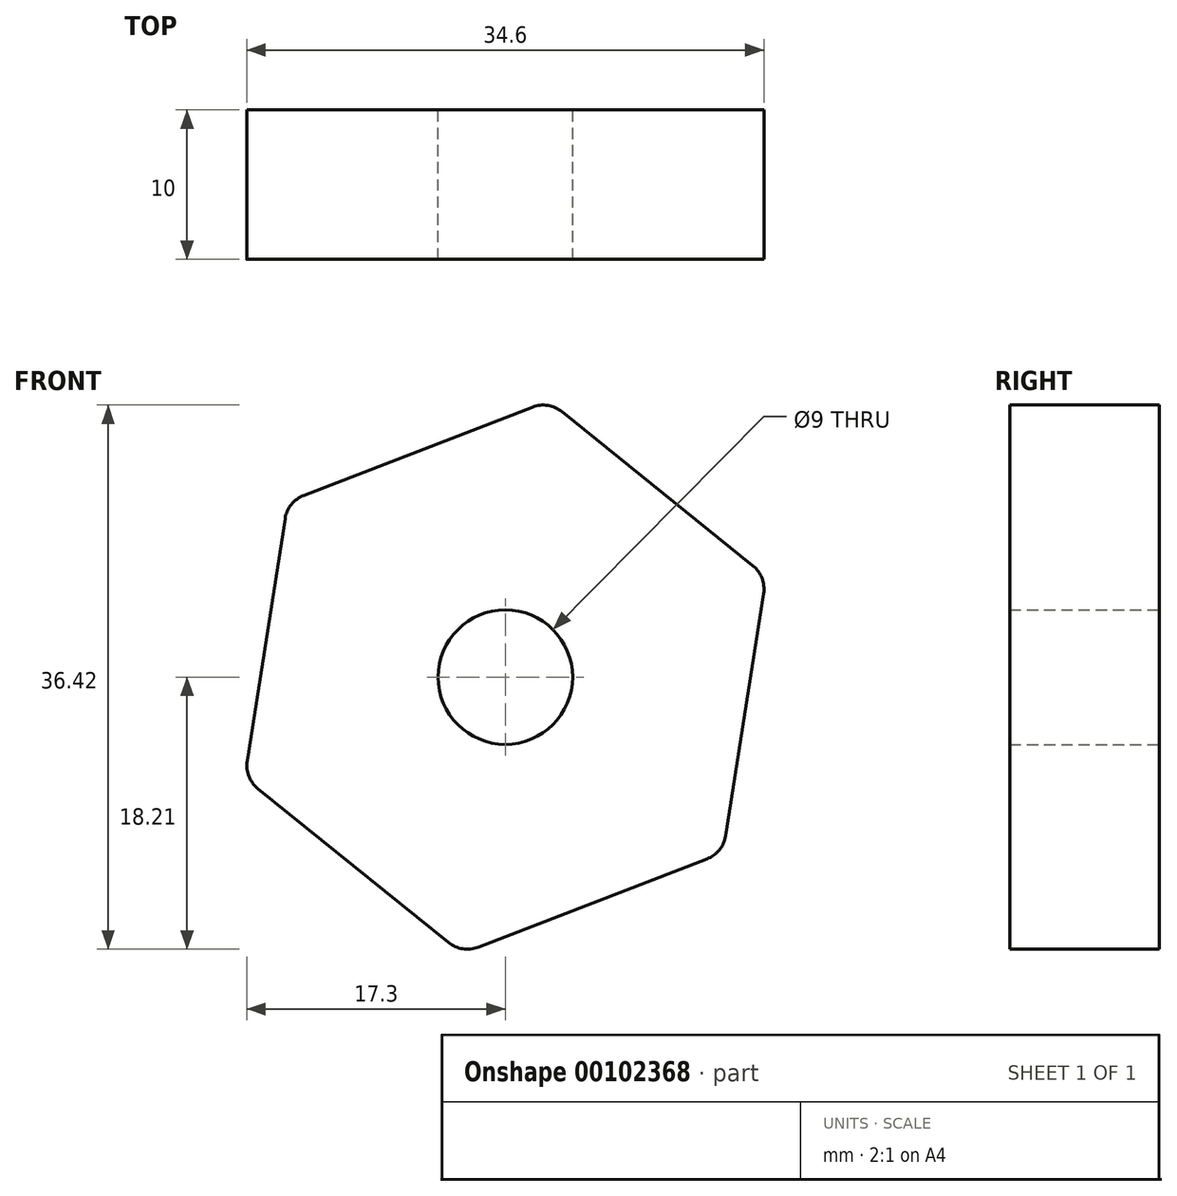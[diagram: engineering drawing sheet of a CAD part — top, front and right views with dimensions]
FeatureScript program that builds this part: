
annotation { "Feature Type Name" : "Feature", "Feature Type Description" : "" }
export const myFeature = defineFeature(function(context is Context, id is Id, definition is map)
    precondition{}
    {
        {
            var Q0;
            Q0=qCreatedBy(makeId("Front.planeOp"),FACE);
            var sketch = newSketch(context, id + "F0", { "sketchPlane" : qUnion([Q0])});
            skCircle(sketch, "E0", {"center": v(0, 0) * mm, "radius": 4.5 * mm});
            skCircle(sketch, "E1.cCircle", {"center": v(0, 0) * mm, "radius": 16.2 * mm, "construction": true});
            skLineSegment(sketch, "E1.0", {"start": v(17.46, 6.74) * mm, "end": v(14.56, -11.75) * mm});
            skLineSegment(sketch, "E1.1", {"start": v(14.56, -11.75) * mm, "end": v(-2.9, -18.49) * mm});
            skLineSegment(sketch, "E1.2", {"start": v(-2.9, -18.49) * mm, "end": v(-17.46, -6.74) * mm});
            skLineSegment(sketch, "E1.3", {"start": v(-17.46, -6.74) * mm, "end": v(-14.56, 11.75) * mm});
            skLineSegment(sketch, "E1.4", {"start": v(-14.56, 11.75) * mm, "end": v(2.9, 18.49) * mm});
            skLineSegment(sketch, "E1.5", {"start": v(2.9, 18.49) * mm, "end": v(17.46, 6.74) * mm});
            skPoint(sketch, "E1.0.midPoint", {"position": v(16.01, -2.5) * mm});
            skSolve(sketch);
        }
        {
            var Q0;
            Q0=makeQuery(id+"F0.imprint","IMPRINT",FACE,{"disambiguationData":[TD([[makeQuery(id+"F0.imprint","IMPRINT",EDGE,{"derivedFrom":sQuery(id+"F0.wireOp",EDGE,"E0")}),-1.0]])]});
            extrude(context, id + "F1", {"entities" : qUnion([Q0]), "depth" : 10 * mm});
        }
        {
            var Q0;
            Q0=makeQuery(id+"F1.opExtrude","SWEPT_EDGE",EDGE,{"disambiguationData":[OSD([sQuery(id+"F0.wireOp",EDGE,"E1.4"),sQuery(id+"F0.wireOp",EDGE,"E1.5")])]});
            var Q1;
            Q1=makeQuery(id+"F1.opExtrude","SWEPT_EDGE",EDGE,{"disambiguationData":[OSD([sQuery(id+"F0.wireOp",EDGE,"E1.0"),sQuery(id+"F0.wireOp",EDGE,"E1.5")])]});
            var Q2;
            Q2=makeQuery(id+"F1.opExtrude","SWEPT_EDGE",EDGE,{"disambiguationData":[OSD([sQuery(id+"F0.wireOp",EDGE,"E1.0"),sQuery(id+"F0.wireOp",EDGE,"E1.1")])]});
            var Q3;
            Q3=makeQuery(id+"F1.opExtrude","SWEPT_EDGE",EDGE,{"disambiguationData":[OSD([sQuery(id+"F0.wireOp",EDGE,"E1.1"),sQuery(id+"F0.wireOp",EDGE,"E1.2")])]});
            var Q4;
            Q4=makeQuery(id+"F1.opExtrude","SWEPT_EDGE",EDGE,{"disambiguationData":[OSD([sQuery(id+"F0.wireOp",EDGE,"E1.2"),sQuery(id+"F0.wireOp",EDGE,"E1.3")])]});
            var Q5;
            Q5=makeQuery(id+"F1.opExtrude","SWEPT_EDGE",EDGE,{"disambiguationData":[OSD([sQuery(id+"F0.wireOp",EDGE,"E1.3"),sQuery(id+"F0.wireOp",EDGE,"E1.4")])]});
            fillet(context, id + "F2", {"entities" : qUnion([Q0, Q1, Q2, Q3, Q4, Q5]), "radius" : 2 * mm, "tangentPropagation" : true, "allowEdgeOverflow" : false});
        }
    });
